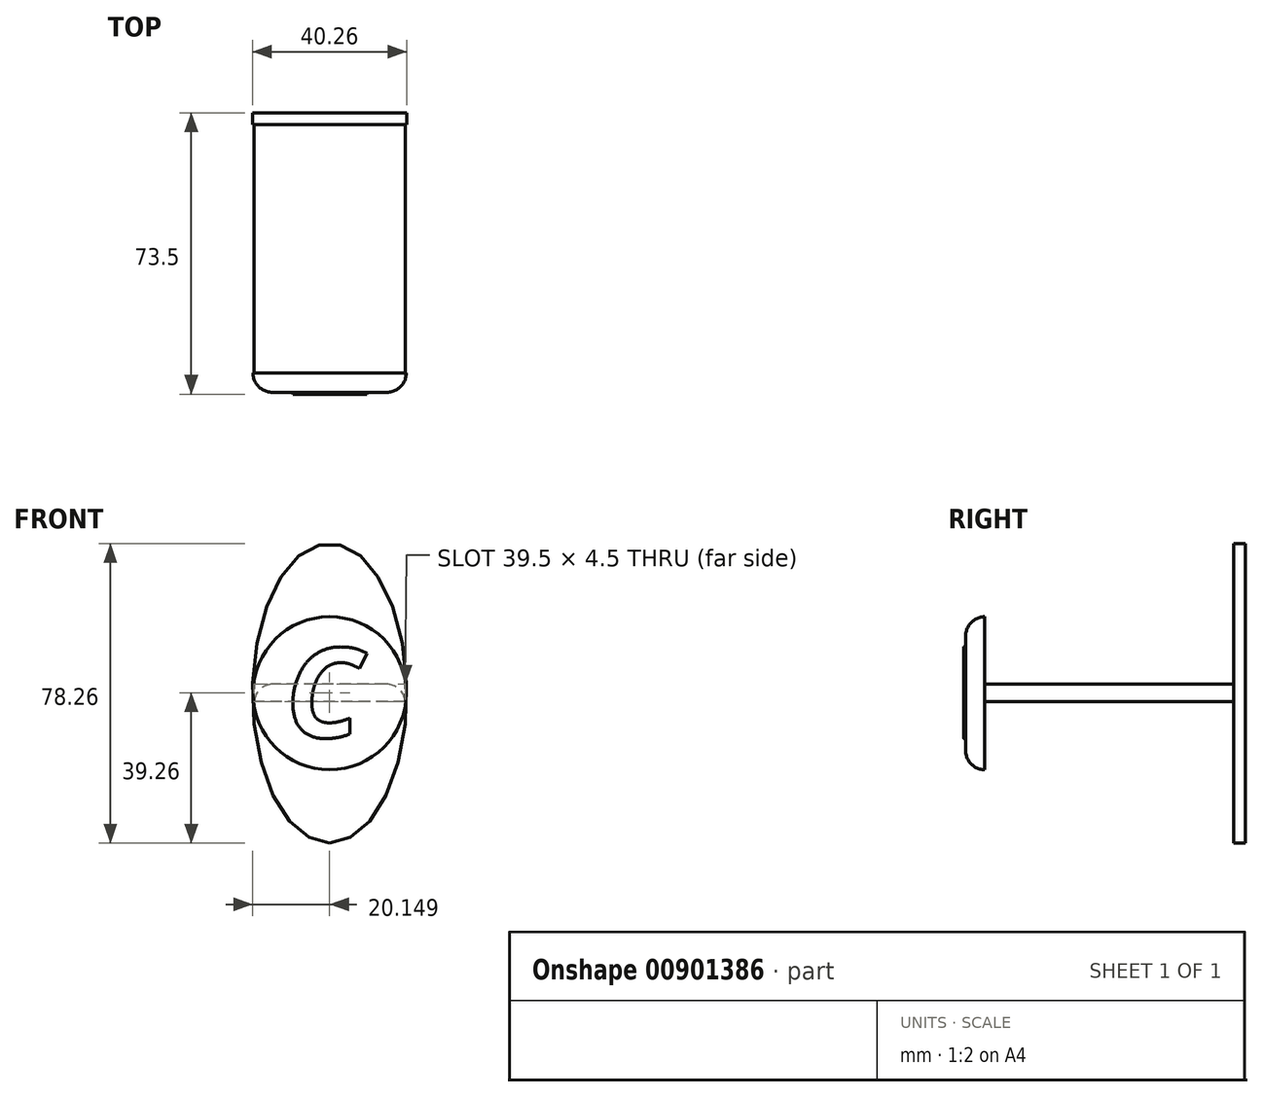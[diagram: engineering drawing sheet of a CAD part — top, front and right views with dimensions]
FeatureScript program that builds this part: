
annotation { "Feature Type Name" : "Feature", "Feature Type Description" : "" }
export const myFeature = defineFeature(function(context is Context, id is Id, definition is map)
    precondition{}
    {
        {
            var Q0;
            Q0=qCreatedBy(makeId("Front.planeOp"),FACE);
            var sketch = newSketch(context, id + "F0", { "sketchPlane" : qUnion([Q0])});
            skCircle(sketch, "E0", {"center": v(0, 0) * mm, "radius": 20 * mm});
            skText(sketch, "E1", { "text": "C", "fontName": "OpenSans-BoldItalic.ttf"});
            const initialGuessF0  = {"E1": [-0.01155, -0.01155, 1, 0, 0.02349]};
            skSetInitialGuess(sketch, initialGuessF0);
            skSolve(sketch);
        }
        {
            var Q0;
            Q0 = qSketchRegion(id + "F0", true);
            extrude(context, id + "F1", {"entities" : qUnion([Q0]), "depth" : 5 * mm, "offsetDistance" : 25 * mm});
        }
        {
            var Q0;
            Q0=makeQuery(id+"F1.opExtrude","CAP_EDGE",EDGE,{"disambiguationData":[OSD([sQuery(id+"F0.wireOp",EDGE,"E0")])],"isStart":false});
            fillet(context, id + "F2", {"entities" : qUnion([Q0]), "radius" : 5 * mm, "tangentPropagation" : true, "allowEdgeOverflow" : false});
        }
        {
            var Q0;
            Q0=makeQuery(id+"F1.opExtrude","CAP_FACE",FACE,{"disambiguationData":[OSD([sQuery(id+"F0.wireOp",EDGE,"E0"),sQuery(id+"F0.wireOp",EDGE,"E1.sketch_text.stroke-0"),sQuery(id+"F0.wireOp",EDGE,"E1.sketch_text.stroke-1"),sQuery(id+"F0.wireOp",EDGE,"E1.sketch_text.stroke-2"),sQuery(id+"F0.wireOp",EDGE,"E1.sketch_text.stroke-3"),sQuery(id+"F0.wireOp",EDGE,"E1.sketch_text.stroke-4"),sQuery(id+"F0.wireOp",EDGE,"E1.sketch_text.stroke-5"),sQuery(id+"F0.wireOp",EDGE,"E1.sketch_text.stroke-6"),sQuery(id+"F0.wireOp",EDGE,"E1.sketch_text.stroke-7"),sQuery(id+"F0.wireOp",EDGE,"E1.sketch_text.stroke-8"),sQuery(id+"F0.wireOp",EDGE,"E1.sketch_text.stroke-9"),sQuery(id+"F0.wireOp",EDGE,"E1.sketch_text.stroke-10"),sQuery(id+"F0.wireOp",EDGE,"E1.sketch_text.stroke-11"),sQuery(id+"F0.wireOp",EDGE,"E1.sketch_text.stroke-12"),sQuery(id+"F0.wireOp",EDGE,"E1.sketch_text.stroke-13"),sQuery(id+"F0.wireOp",EDGE,"E1.sketch_text.stroke-14"),sQuery(id+"F0.wireOp",EDGE,"E1.sketch_text.stroke-15"),sQuery(id+"F0.wireOp",EDGE,"E1.sketch_text.stroke-16"),sQuery(id+"F0.wireOp",EDGE,"E1.sketch_text.stroke-17")])],"isStart":true});
            cPlane(context, id + "F3", {"entities" : qUnion([Q0]), "cplaneType" : CPlaneType.OFFSET, "offset" : 0 * mm, "width" : 150 * mm, "height" : 150 * mm});
        }
        {
            var Q0;
            Q0=makeQuery(id+"F0.imprint","IMPRINT",FACE,{"disambiguationData":[TD([[makeQuery(id+"F0.imprint","IMPRINT",EDGE,{"derivedFrom":sQuery(id+"F0.wireOp",EDGE,"E1.sketch_text.stroke-0")}),-1.0]])]});
            extrude(context, id + "F4", {"entities" : qUnion([Q0]), "operationType" : NewBodyOperationType.ADD, "depth" : 5.5 * mm, "offsetDistance" : 25 * mm});
        }
        {
            var Q0;
            Q0=qCreatedBy(id+"F3.planeOp",FACE);
            var sketch = newSketch(context, id + "F5", { "sketchPlane" : qUnion([Q0])});
            skLineSegment(sketch, "E2.bottom", {"start": v(-19.77, 2.38) * mm, "end": v(19.73, 2.38) * mm});
            skLineSegment(sketch, "E2.top", {"start": v(-19.77, -2.12) * mm, "end": v(19.73, -2.12) * mm});
            skLineSegment(sketch, "E2.left", {"start": v(-19.77, 2.38) * mm, "end": v(-19.77, -2.12) * mm});
            skLineSegment(sketch, "E2.right", {"start": v(19.73, 2.38) * mm, "end": v(19.73, -2.12) * mm});
            skSolve(sketch);
        }
        {
            var Q0;
            Q0 = qSketchRegion(id + "F5", true);
            extrude(context, id + "F6", {"entities" : qUnion([Q0]), "operationType" : NewBodyOperationType.ADD, "depth" : 65 * mm, "offsetDistance" : 25 * mm});
        }
        {
            var Q0;
            Q0=makeQuery(id+"F6.opExtrude","SWEPT_EDGE",EDGE,{"disambiguationData":[OSD([sQuery(id+"F5.wireOp",EDGE,"E2.bottom"),sQuery(id+"F5.wireOp",EDGE,"E2.left")])]});
            var Q1;
            Q1=makeQuery(id+"F6.opExtrude","SWEPT_EDGE",EDGE,{"disambiguationData":[OSD([sQuery(id+"F5.wireOp",EDGE,"E2.bottom"),sQuery(id+"F5.wireOp",EDGE,"E2.right")])]});
            fillet(context, id + "F7", {"entities" : qUnion([Q0, Q1]), "radius" : 5 * mm, "tangentPropagation" : true, "allowEdgeOverflow" : false});
        }
        {
            var Q0;
            Q0=makeQuery(id+"F6.opExtrude","CAP_FACE",FACE,{"disambiguationData":[OSD([sQuery(id+"F5.wireOp",EDGE,"E2.bottom"),sQuery(id+"F5.wireOp",EDGE,"E2.top"),sQuery(id+"F5.wireOp",EDGE,"E2.left"),sQuery(id+"F5.wireOp",EDGE,"E2.right")])],"isStart":false});
            cPlane(context, id + "F8", {"entities" : qUnion([Q0]), "cplaneType" : CPlaneType.OFFSET, "offset" : 0 * mm, "width" : 150 * mm, "height" : 150 * mm});
        }
        {
            var Q0;
            Q0=qCreatedBy(id+"F8.planeOp",FACE);
            var sketch = newSketch(context, id + "F9", { "sketchPlane" : qUnion([Q0])});
            skEllipse(sketch, "E3", {"center": v(0, 0) * mm, "majorRadius": 39.13 * mm, "minorRadius": 20.13 * mm, "majorAxis": v(0, -1)});
            skSolve(sketch);
        }
        {
            var Q0;
            Q0 = qSketchRegion(id + "F9", true);
            extrude(context, id + "F10", {"entities" : qUnion([Q0]), "operationType" : NewBodyOperationType.ADD, "depth" : 3 * mm, "offsetDistance" : 25 * mm});
        }
        {
            var Q0;
            Q0=makeQuery(id+"F10.opExtrude","CAP_FACE",FACE,{"disambiguationData":[OSD([sQuery(id+"F9.wireOp",EDGE,"E3")])],"isStart":false});
            cPlane(context, id + "F11", {"entities" : qUnion([Q0]), "cplaneType" : CPlaneType.OFFSET, "offset" : 0 * mm, "width" : 150 * mm, "height" : 150 * mm});
        }
    });
